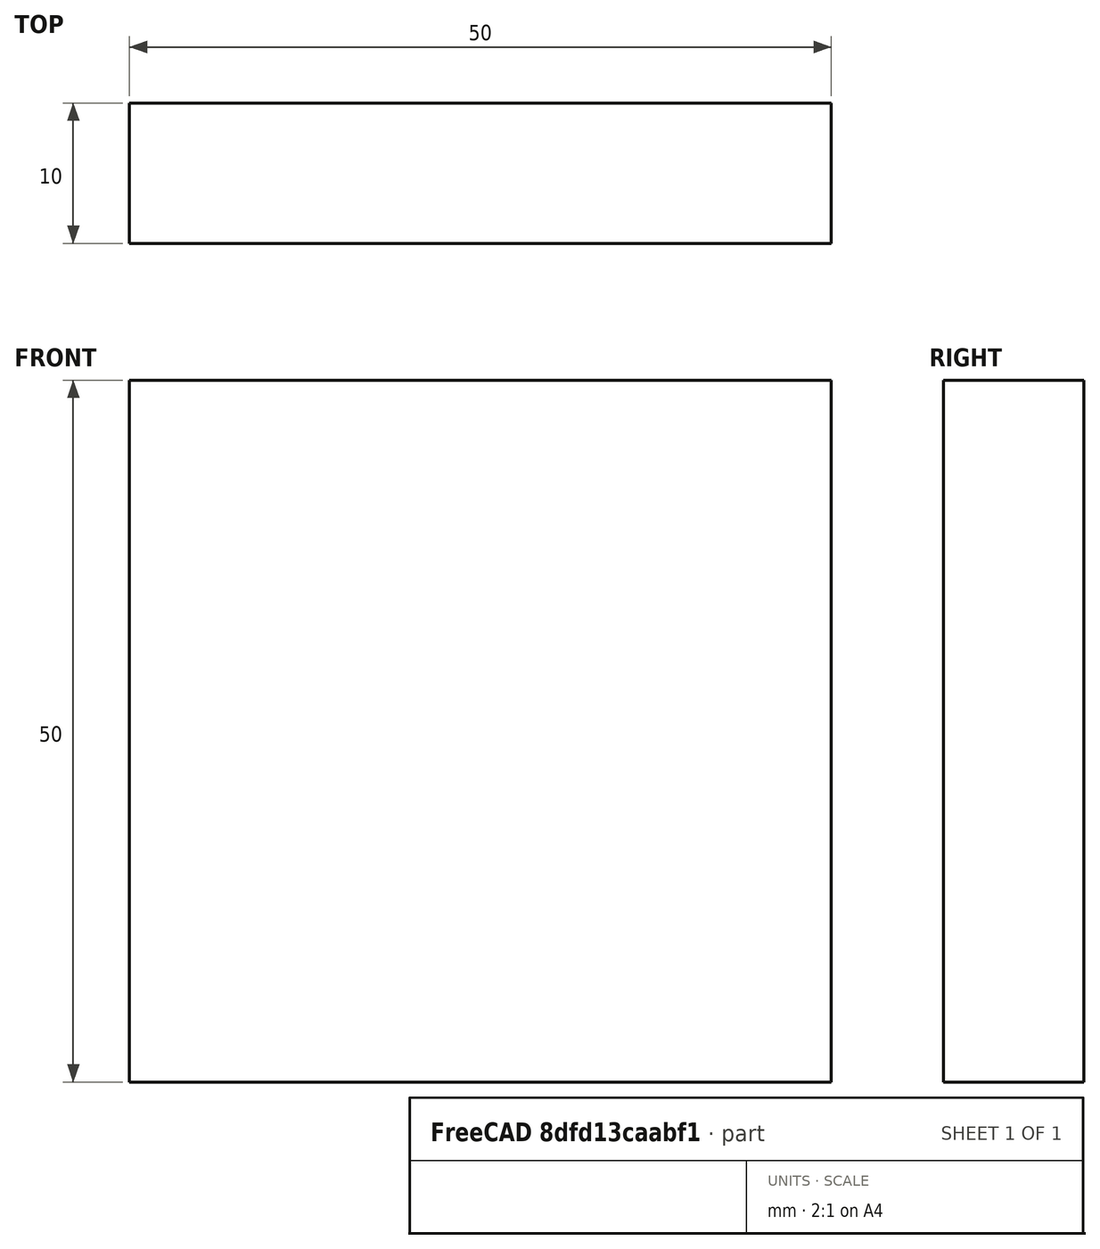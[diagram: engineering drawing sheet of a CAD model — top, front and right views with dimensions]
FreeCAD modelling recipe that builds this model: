
FCSTD DOCUMENT  (FreeCAD 0.15R4671 (Git))
Label: Flat Bar 50x10 EN10058 S235JR
License: All rights reserved
LicenseURL: http://en.wikipedia.org/wiki/All_rights_reserved
objects: Sketcher::SketchObject×1, Part::Extrusion×1
note: 2 computed .brp shape members not serialized (recipe doc carries the construction recipe); baked Part::Feature solids carry a one-line shape summary decoded from their .brp

FEATURE [Sketcher::SketchObject] Sketch
  sketch-geometry (4):
    g0: LineSegment StartX=-25 StartY=-5 StartZ=0 EndX=25 EndY=-5 EndZ=0
    g1: LineSegment StartX=25 StartY=-5 StartZ=0 EndX=25 EndY=5 EndZ=0
    g2: LineSegment StartX=25 StartY=5 StartZ=0 EndX=-25 EndY=5 EndZ=0
    g3: LineSegment StartX=-25 StartY=5 StartZ=0 EndX=-25 EndY=-5 EndZ=0
  constraints (12):
    c: Coincident(g0,g1)
    c: Coincident(g1,g2)
    c: Coincident(g2,g3)
    c: Coincident(g3,g0)
    c: Horizontal(g0)
    c: Horizontal(g2)
    c: Vertical(g1)
    c: Vertical(g3)
    c: Symmetric(g1,g2,g-2)
    c: Symmetric(g0,g1,g-1)
    c: DistanceY(g1) = 10
    c: DistanceX(g0) = 50
FEATURE [Part::Extrusion] Extrude  label="Flat Bar 50x10 EN10058 S235JR"
  Base = -> Sketch
  Dir = (0,0,50)
  Solid = true
